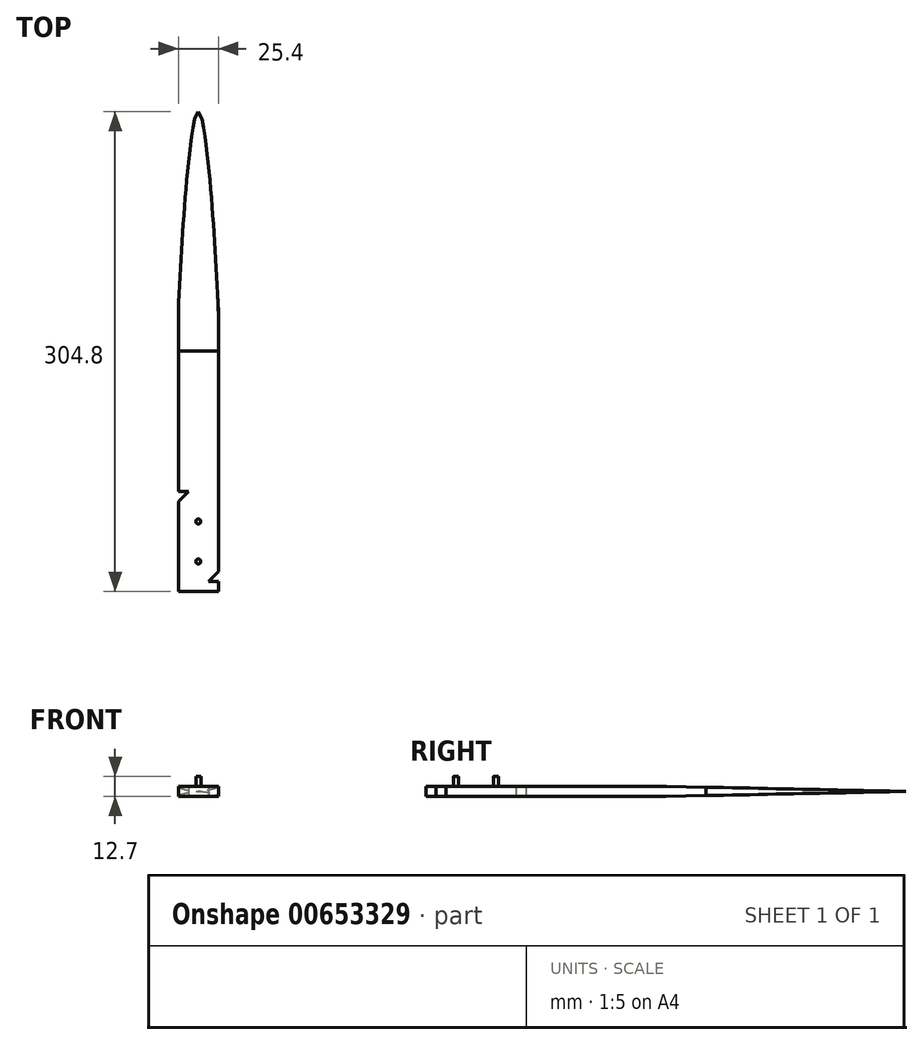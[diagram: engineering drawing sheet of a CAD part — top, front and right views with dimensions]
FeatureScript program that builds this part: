
annotation { "Feature Type Name" : "Feature", "Feature Type Description" : "" }
export const myFeature = defineFeature(function(context is Context, id is Id, definition is map)
    precondition{}
    {
        {
            var Q0;
            Q0=qCreatedBy(makeId("Top.planeOp"),FACE);
            var sketch = newSketch(context, id + "F0", { "sketchPlane" : qUnion([Q0])});
            skLineSegment(sketch, "E0.bottom", {"start": v(12.7, -152.4) * mm, "end": v(-12.7, -152.4) * mm});
            skLineSegment(sketch, "E0.top", {"start": v(12.7, 152.4) * mm, "end": v(-12.7, 152.4) * mm});
            skLineSegment(sketch, "E0.left", {"start": v(12.7, -152.4) * mm, "end": v(12.7, 152.4) * mm});
            skLineSegment(sketch, "E0.right", {"start": v(-12.7, -152.4) * mm, "end": v(-12.7, 152.4) * mm});
            skPoint(sketch, "E0.middle", {"position": v(0, 0) * mm});
            skCircle(sketch, "E1", {"center": v(0, -133.35) * mm, "radius": 1.59 * mm});
            skFitSpline(sketch, "E2", {"points": [v(12.7, 0) * mm, v(12.7, 25.4) * mm, v(0, 152.4) * mm, v(-12.7, 25.4) * mm, v(-12.7, 0) * mm], "startDerivative": vector(0, 270.17) * mm, "endDerivative": vector(0, -264) * mm});
            skCircle(sketch, "E3", {"center": v(0, -107.95) * mm, "radius": 1.59 * mm});
            skLineSegment(sketch, "E4", {"start": v(0, -107.95) * mm, "end": v(12.7, -107.95) * mm, "construction": true});
            skLineSegment(sketch, "E5", {"start": v(12.7, -107.95) * mm, "end": v(-12.7, -107.95) * mm, "construction": true});
            skLineSegment(sketch, "E6", {"start": v(0, -133.35) * mm, "end": v(12.7, -133.35) * mm, "construction": true});
            skLineSegment(sketch, "E7", {"start": v(12.7, -133.35) * mm, "end": v(-12.7, -133.35) * mm, "construction": true});
            skLineSegment(sketch, "E8", {"start": v(-12.7, -88.9) * mm, "end": v(-6.35, -88.9) * mm});
            skLineSegment(sketch, "E9", {"start": v(-6.35, -88.9) * mm, "end": v(-12.7, -95.25) * mm});
            skLineSegment(sketch, "E10", {"start": v(12.7, -146.05) * mm, "end": v(6.35, -146.05) * mm});
            skLineSegment(sketch, "E11", {"start": v(6.35, -146.05) * mm, "end": v(12.7, -139.7) * mm});
            skSolve(sketch);
        }
        {
            var Q0;
            Q0=makeQuery(id+"F0.imprint","IMPRINT",FACE,{"disambiguationData":[TD([[makeQuery(id+"F0.imprint","IMPRINT",EDGE,{"derivedFrom":sQuery(id+"F0.wireOp",EDGE,"E1")}),1.0]])]});
            var Q1;
            {var subQ1=sQuery(id+"F0.wireOp",EDGE,"E0.bottom");Q1=makeQuery(id+"F0.imprint","IMPRINT",FACE,{"disambiguationData":[TD([[makeQuery(id+"F0.imprint","IMPRINT",EDGE,{"derivedFrom":subQ1}),-1.0]])]});}
            extrude(context, id + "F1", {"entities" : qUnion([Q0, Q1]), "depth" : 6.35 * mm, "offsetDistance" : 25.4 * mm});
        }
        {
            var Q0;
            Q0=makeQuery(id+"F0.imprint","IMPRINT",FACE,{"disambiguationData":[TD([[makeQuery(id+"F0.imprint","IMPRINT",EDGE,{"derivedFrom":sQuery(id+"F0.wireOp",EDGE,"E1")}),1.0]])]});
            extrude(context, id + "F2", {"entities" : qUnion([Q0]), "operationType" : NewBodyOperationType.ADD, "depth" : 12.7 * mm, "offsetDistance" : 25.4 * mm});
        }
        {
            var Q0;
            Q0=makeQuery(id+"F0.imprint","IMPRINT",FACE,{"disambiguationData":[TD([[makeQuery(id+"F0.imprint","IMPRINT",EDGE,{"derivedFrom":sQuery(id+"F0.wireOp",EDGE,"E3")}),1.0]])]});
            extrude(context, id + "F3", {"entities" : qUnion([Q0]), "operationType" : NewBodyOperationType.ADD, "depth" : 12.7 * mm, "offsetDistance" : 25.4 * mm});
        }
        {
            var Q0;
            {var subQ0=sQuery(id+"F0.wireOp",EDGE,"E8");Q0=makeQuery(id+"F0.imprint","IMPRINT",FACE,{"disambiguationData":[TD([[makeQuery(id+"F0.imprint","IMPRINT",EDGE,{"derivedFrom":subQ0}),-1.0]])]});}
            var Q1;
            {var subQ0=sQuery(id+"F0.wireOp",EDGE,"E10");Q1=makeQuery(id+"F0.imprint","IMPRINT",FACE,{"disambiguationData":[TD([[makeQuery(id+"F0.imprint","IMPRINT",EDGE,{"derivedFrom":subQ0}),-1.0]])]});}
            extrude(context, id + "F4", {"entities" : qUnion([Q0, Q1]), "operationType" : NewBodyOperationType.REMOVE, "depth" : 25.4 * mm, "offsetDistance" : 25.4 * mm});
        }
        {
            var Q0;
            Q0=qCreatedBy(makeId("Right.planeOp"),FACE);
            var sketch = newSketch(context, id + "F5", { "sketchPlane" : qUnion([Q0])});
            skPoint(sketch, "E12", {"position": v(0, 6.36) * mm});
            skPoint(sketch, "E13", {"position": v(152.4, 0) * mm});
            skPoint(sketch, "E14", {"position": v(152.4, 6.35) * mm});
            skLineSegment(sketch, "E15", {"start": v(0, 6.36) * mm, "end": v(152.4, 3.18) * mm});
            skLineSegment(sketch, "E16", {"start": v(152.4, 3.18) * mm, "end": v(152.4, 3.18) * mm});
            skLineSegment(sketch, "E17", {"start": v(0, 0) * mm, "end": v(152.4, 3.18) * mm});
            skLineSegment(sketch, "E18", {"start": v(0, 6.36) * mm, "end": v(152.4, 6.35) * mm});
            skLineSegment(sketch, "E19", {"start": v(152.4, 6.35) * mm, "end": v(152.4, 0) * mm});
            skLineSegment(sketch, "E20", {"start": v(152.4, 0) * mm, "end": v(0, 0) * mm});
            skSolve(sketch);
        }
        {
            var Q0;
            Q0 = qSketchRegion(id + "F5", true);
            extrude(context, id + "F6", {"entities" : qUnion([Q0]), "operationType" : NewBodyOperationType.REMOVE, "oppositeDirection" : true, "depth" : 25.4 * mm, "offsetDistance" : 25.4 * mm, "hasSecondDirection" : true, "secondDirectionOppositeDirection" : false, "secondDirectionDepth" : 25.4 * mm});
        }
    });
